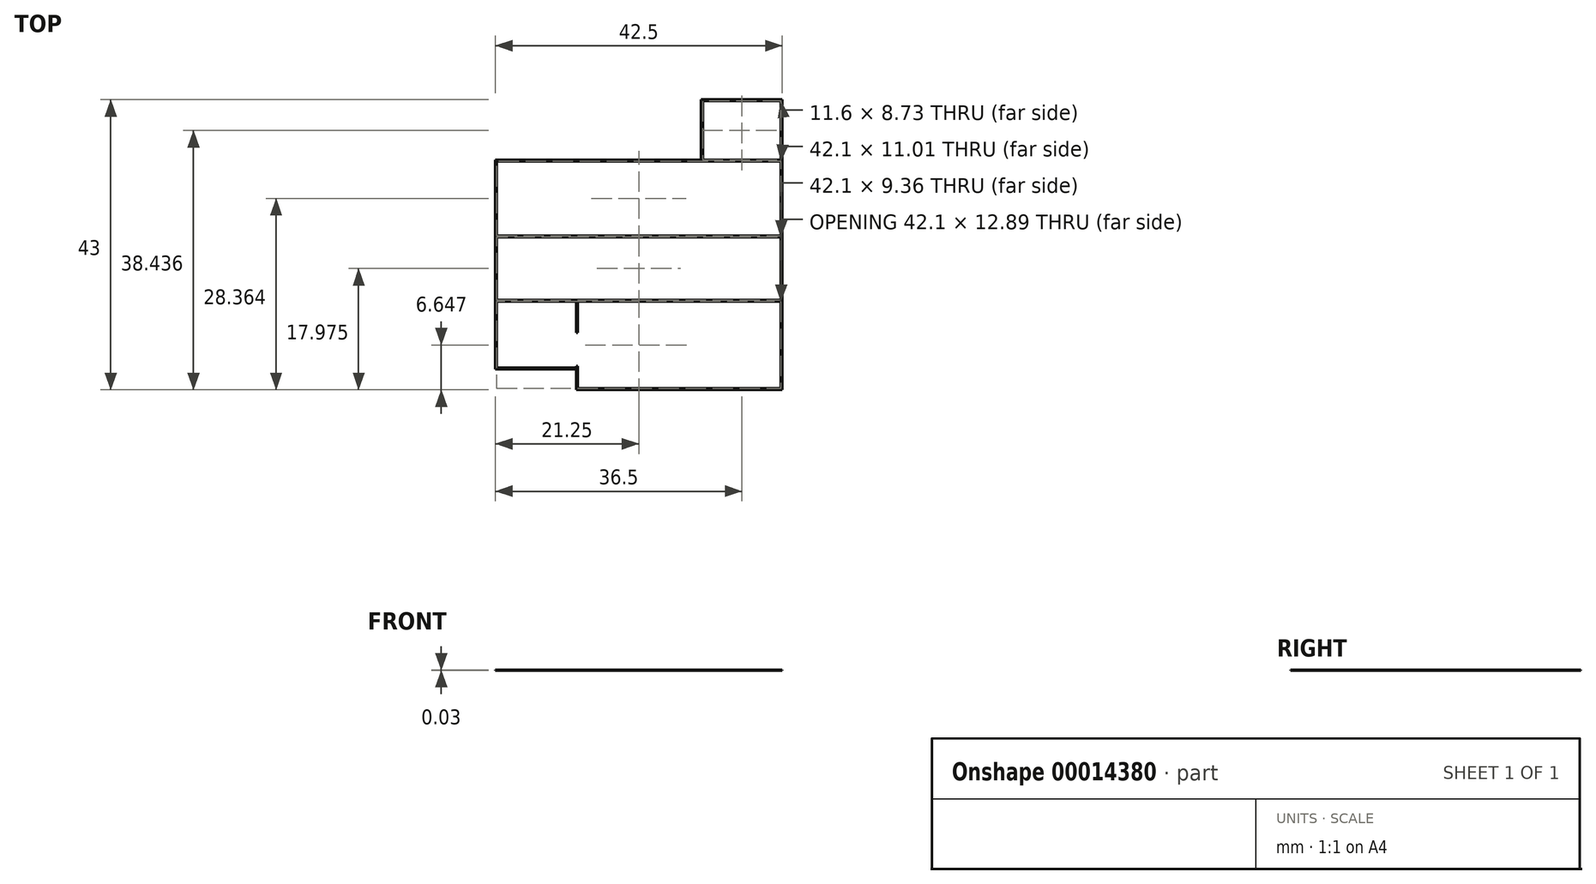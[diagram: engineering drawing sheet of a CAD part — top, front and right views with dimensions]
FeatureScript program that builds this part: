
annotation { "Feature Type Name" : "Feature", "Feature Type Description" : "" }
export const myFeature = defineFeature(function(context is Context, id is Id, definition is map)
    precondition{}
    {
        {
            var Q0;
            Q0=qCreatedBy(makeId("Top.planeOp"),FACE);
            var sketch = newSketch(context, id + "F0", { "sketchPlane" : qUnion([Q0])});
            skLineSegment(sketch, "E0.bottom", {"start": v(-42.5, 34.07) * mm, "end": v(-12, 34.07) * mm});
            skLineSegment(sketch, "E0.top", {"start": v(-42.3, 13.1) * mm, "end": v(-30.5, 13.1) * mm});
            skLineSegment(sketch, "E1", {"start": v(-42.5, 34.07) * mm, "end": v(-42.5, 3.07) * mm});
            skLineSegment(sketch, "E2", {"start": v(-42.5, 3.07) * mm, "end": v(-30.5, 3.07) * mm});
            skLineSegment(sketch, "E3", {"start": v(-30.5, 13.1) * mm, "end": v(-30.5, 8.5) * mm});
            skLineSegment(sketch, "E4", {"start": v(-30.5, 0) * mm, "end": v(0, 0) * mm});
            skLineSegment(sketch, "E5", {"start": v(0, 0) * mm, "end": v(0, 43) * mm});
            skLineSegment(sketch, "E6", {"start": v(0, 43) * mm, "end": v(-12, 43) * mm});
            skLineSegment(sketch, "E7", {"start": v(-12, 43) * mm, "end": v(-12, 34.07) * mm});
            skLineSegment(sketch, "E8.bottom", {"start": v(-11.8, 42.8) * mm, "end": v(-0.2, 42.8) * mm});
            skLineSegment(sketch, "E8.top", {"start": v(-11.8, 34.07) * mm, "end": v(-0.2, 34.07) * mm});
            skLineSegment(sketch, "E8.left", {"start": v(-11.8, 42.8) * mm, "end": v(-11.8, 34.07) * mm});
            skLineSegment(sketch, "E8.right", {"start": v(-0.2, 42.8) * mm, "end": v(-0.2, 34.07) * mm});
            skLineSegment(sketch, "E9.bottom", {"start": v(-0.2, 22.86) * mm, "end": v(-42.3, 22.86) * mm});
            skLineSegment(sketch, "E9.top", {"start": v(-0.2, 33.87) * mm, "end": v(-42.3, 33.87) * mm});
            skLineSegment(sketch, "E9.left", {"start": v(-0.2, 22.86) * mm, "end": v(-0.2, 33.87) * mm});
            skLineSegment(sketch, "E9.right", {"start": v(-42.3, 22.86) * mm, "end": v(-42.3, 33.87) * mm});
            skLineSegment(sketch, "E10.bottom", {"start": v(-42.3, 22.66) * mm, "end": v(-0.2, 22.66) * mm});
            skLineSegment(sketch, "E10.top", {"start": v(-42.3, 13.3) * mm, "end": v(-0.2, 13.3) * mm});
            skLineSegment(sketch, "E10.left", {"start": v(-42.3, 22.66) * mm, "end": v(-42.3, 13.3) * mm});
            skLineSegment(sketch, "E10.right", {"start": v(-0.2, 22.66) * mm, "end": v(-0.2, 13.3) * mm});
            skLineSegment(sketch, "E11", {"start": v(-42.3, 13.1) * mm, "end": v(-42.3, 3.27) * mm});
            skLineSegment(sketch, "E12", {"start": v(-42.3, 3.27) * mm, "end": v(-30.5, 3.27) * mm});
            skLineSegment(sketch, "E13", {"start": v(-30.3, 0.2) * mm, "end": v(-0.2, 0.2) * mm});
            skLineSegment(sketch, "E14", {"start": v(-0.2, 13.1) * mm, "end": v(-0.2, 0.2) * mm});
            skLineSegment(sketch, "E15.trimOffspring", {"start": v(-30.5, 3.07) * mm, "end": v(-30.5, 0) * mm});
            skLineSegment(sketch, "E16", {"start": v(-30.3, 0.2) * mm, "end": v(-30.3, 3.5) * mm});
            skLineSegment(sketch, "E17.trimOffspring", {"start": v(-30.3, 13.1) * mm, "end": v(-0.2, 13.1) * mm});
            skLineSegment(sketch, "E18", {"start": v(-30.5, 3.5) * mm, "end": v(-30.3, 3.5) * mm});
            skLineSegment(sketch, "E19", {"start": v(-30.5, 8.5) * mm, "end": v(-30.3, 8.5) * mm});
            skLineSegment(sketch, "E20.trimOffspring", {"start": v(-30.3, 8.5) * mm, "end": v(-30.3, 13.1) * mm});
            skLineSegment(sketch, "E21.trimOffspring", {"start": v(-30.5, 3.5) * mm, "end": v(-30.5, 3.27) * mm});
            skSolve(sketch);
        }
        {
            var Q0;
            Q0=qSketchRegion(id+"F0",true);
            extrude(context, id + "F1", {"entities" : qUnion([Q0]), "depth" : 0.03 * mm});
        }
    });
